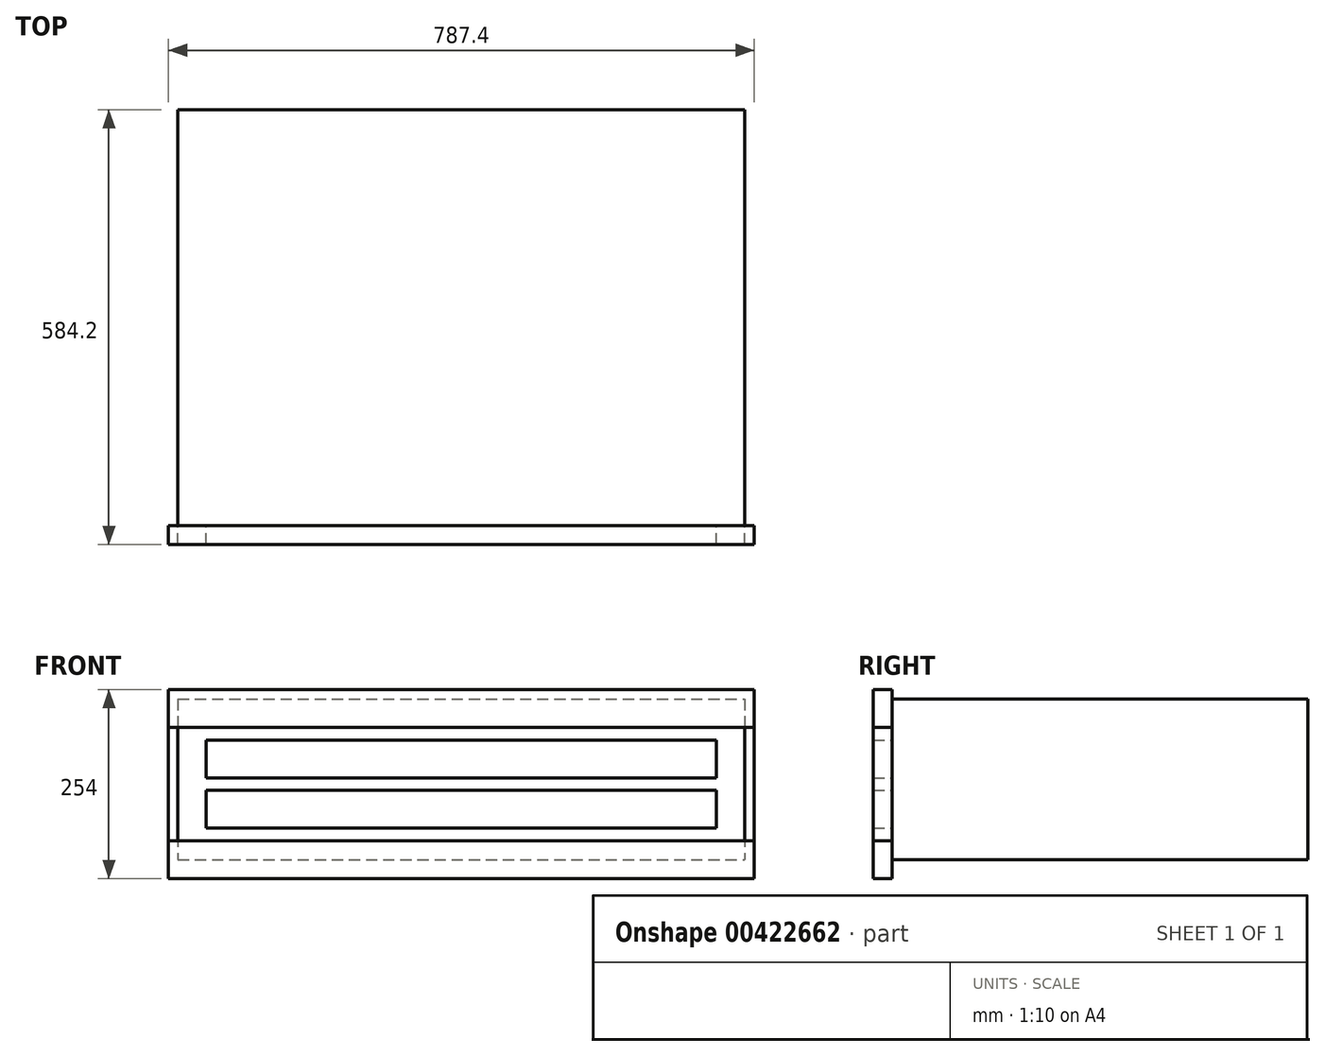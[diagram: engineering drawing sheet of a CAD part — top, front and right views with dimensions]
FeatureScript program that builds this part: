
annotation { "Feature Type Name" : "Feature", "Feature Type Description" : "" }
export const myFeature = defineFeature(function(context is Context, id is Id, definition is map)
    precondition{}
    {
        {
            var Q0;
            Q0=qCreatedBy(makeId("Front.planeOp"),FACE);
            var sketch = newSketch(context, id + "F0", { "sketchPlane" : qUnion([Q0])});
            skLineSegment(sketch, "E0.bottom", {"start": v(0, 0) * mm, "end": v(774.7, 0) * mm, "construction": true});
            skLineSegment(sketch, "E0.top", {"start": v(0, 279.4) * mm, "end": v(774.7, 279.4) * mm, "construction": true});
            skLineSegment(sketch, "E0.left", {"start": v(0, 0) * mm, "end": v(0, 279.4) * mm, "construction": true});
            skLineSegment(sketch, "E0.right", {"start": v(774.7, 0) * mm, "end": v(774.7, 279.4) * mm, "construction": true});
            skLineSegment(sketch, "E1", {"start": v(0, 50.8) * mm, "end": v(774.7, 50.8) * mm});
            skLineSegment(sketch, "E2", {"start": v(0, 266.7) * mm, "end": v(774.7, 266.7) * mm});
            skLineSegment(sketch, "E3", {"start": v(774.7, 266.7) * mm, "end": v(768.35, 266.7) * mm, "construction": true});
            skLineSegment(sketch, "E4", {"start": v(768.35, 266.7) * mm, "end": v(768.35, 50.8) * mm});
            skLineSegment(sketch, "E5", {"start": v(6.35, 266.7) * mm, "end": v(6.35, 50.8) * mm});
            skSolve(sketch);
        }
        {
            var Q0;
            {var subQ0=sQuery(id+"F0.wireOp",EDGE,"E4");Q0=makeQuery(id+"F0.imprint","IMPRINT",FACE,{"disambiguationData":[TD([[makeQuery(id+"F0.imprint","IMPRINT",EDGE,{"derivedFrom":subQ0}),-1.0]])]});}
            var Q1;
            Q1=sQuery(id+"F0.wireOp",EDGE,"E5");
            var Q2;
            Q2=sQuery(id+"F0.wireOp",EDGE,"E2");
            var Q3;
            Q3=sQuery(id+"F0.wireOp",EDGE,"E1");
            var Q4;
            Q4=sQuery(id+"F0.wireOp",EDGE,"E4");
            extrude(context, id + "F1", {"entities" : qUnion([Q0]), "surfaceEntities" : qUnion([Q1, Q2, Q3, Q4]), "oppositeDirection" : true, "depth" : 558.8 * mm});
        }
        {
            var Q0;
            Q0=makeQuery(id+"F1.opExtrude","CAP_FACE",FACE,{"disambiguationData":[OSD([sQuery(id+"F0.wireOp",EDGE,"E1"),sQuery(id+"F0.wireOp",EDGE,"E2"),sQuery(id+"F0.wireOp",EDGE,"E4"),sQuery(id+"F0.wireOp",EDGE,"E5")])],"isStart":true});
            var sketch = newSketch(context, id + "F2", { "sketchPlane" : qUnion([Q0])});
            skLineSegment(sketch, "E6.bottom", {"start": v(-6.35, 228.6) * mm, "end": v(781.05, 228.6) * mm});
            skLineSegment(sketch, "E6.top", {"start": v(-6.35, 279.4) * mm, "end": v(781.05, 279.4) * mm});
            skLineSegment(sketch, "E6.left", {"start": v(-6.35, 228.6) * mm, "end": v(-6.35, 279.4) * mm});
            skLineSegment(sketch, "E6.right", {"start": v(781.05, 228.6) * mm, "end": v(781.05, 279.4) * mm});
            skLineSegment(sketch, "E7.bottom", {"start": v(44.45, 211.67) * mm, "end": v(730.25, 211.67) * mm});
            skLineSegment(sketch, "E7.top", {"start": v(44.45, 160.87) * mm, "end": v(730.25, 160.87) * mm});
            skLineSegment(sketch, "E7.left", {"start": v(44.45, 211.67) * mm, "end": v(44.45, 160.87) * mm});
            skLineSegment(sketch, "E7.right", {"start": v(730.25, 211.67) * mm, "end": v(730.25, 160.87) * mm});
            skLineSegment(sketch, "E8.bottom", {"start": v(44.45, 143.93) * mm, "end": v(730.25, 143.93) * mm});
            skLineSegment(sketch, "E8.top", {"start": v(44.45, 93.13) * mm, "end": v(730.25, 93.13) * mm});
            skLineSegment(sketch, "E8.left", {"start": v(44.45, 143.93) * mm, "end": v(44.45, 93.13) * mm});
            skLineSegment(sketch, "E8.right", {"start": v(730.25, 143.93) * mm, "end": v(730.25, 93.13) * mm});
            skLineSegment(sketch, "E9.bottom", {"start": v(-6.35, 76.2) * mm, "end": v(781.05, 76.2) * mm});
            skLineSegment(sketch, "E9.top", {"start": v(-6.35, 25.4) * mm, "end": v(781.05, 25.4) * mm});
            skLineSegment(sketch, "E9.left", {"start": v(-6.35, 76.2) * mm, "end": v(-6.35, 25.4) * mm});
            skLineSegment(sketch, "E9.right", {"start": v(781.05, 76.2) * mm, "end": v(781.05, 25.4) * mm});
            skLineSegment(sketch, "E10", {"start": v(387.35, 228.6) * mm, "end": v(387.35, 211.67) * mm, "construction": true});
            skLineSegment(sketch, "E11", {"start": v(387.35, 160.87) * mm, "end": v(387.35, 143.93) * mm, "construction": true});
            skLineSegment(sketch, "E12", {"start": v(387.35, 93.13) * mm, "end": v(387.35, 76.2) * mm, "construction": true});
            skLineSegment(sketch, "E13.bottom", {"start": v(-6.35, 228.6) * mm, "end": v(44.45, 228.6) * mm});
            skLineSegment(sketch, "E13.top", {"start": v(-6.35, 76.2) * mm, "end": v(44.45, 76.2) * mm});
            skLineSegment(sketch, "E13.left", {"start": v(-6.35, 228.6) * mm, "end": v(-6.35, 76.2) * mm});
            skLineSegment(sketch, "E13.right", {"start": v(44.45, 228.6) * mm, "end": v(44.45, 76.2) * mm});
            skLineSegment(sketch, "E14.bottom", {"start": v(781.05, 76.2) * mm, "end": v(730.25, 76.2) * mm});
            skLineSegment(sketch, "E14.top", {"start": v(781.05, 228.6) * mm, "end": v(730.25, 228.6) * mm});
            skLineSegment(sketch, "E14.left", {"start": v(781.05, 76.2) * mm, "end": v(781.05, 228.6) * mm});
            skLineSegment(sketch, "E14.right", {"start": v(730.25, 76.2) * mm, "end": v(730.25, 228.6) * mm});
            skSolve(sketch);
        }
        {
            var Q0;
            Q0=makeQuery(id+"F2.imprint","IMPRINT",FACE,{"disambiguationData":[TD([[makeQuery(id+"F2.imprint","IMPRINT",EDGE,{"derivedFrom":sQuery(id+"F2.wireOp",EDGE,"E6.top")}),-1.0]])]});
            var Q1;
            {var subQ1=sQuery(id+"F2.wireOp",EDGE,"E6.bottom");Q1=makeQuery(id+"F2.imprint","IMPRINT",FACE,{"disambiguationData":[TD([[makeQuery(id+"F2.imprint","IMPRINT",EDGE,{"derivedFrom":subQ1}),1.0]])]});}
            extrude(context, id + "F3", {"entities" : qUnion([Q0, Q1]), "depth" : 25.4 * mm});
        }
        {
            var Q0;
            {var subQ0=sQuery(id+"F2.wireOp",EDGE,"E14.left");Q0=makeQuery(id+"F2.imprint","IMPRINT",FACE,{"disambiguationData":[TD([[makeQuery(id+"F2.imprint","IMPRINT",EDGE,{"derivedFrom":subQ0}),1.0]])]});}
            var Q1;
            {var subQ0=sQuery(id+"F2.wireOp",EDGE,"E14.right");var subQ9=makeQuery(id+"F2.imprint","INTERSECT",VERTEX,{"derivedFrom":[sQuery(id+"F2.wireOp",EDGE,"E8.bottom"),subQ0]});Q1=makeQuery(id+"F2.imprint","IMPRINT",FACE,{"disambiguationData":[TD([[makeQuery(id+"F2.imprint","IMPRINT",EDGE,{"disambiguationData":[TD([[subQ9,1.0]])],"derivedFrom":subQ0}),-1.0]])]});}
            extrude(context, id + "F4", {"entities" : qUnion([Q0, Q1]), "depth" : 25.4 * mm});
        }
        {
            var Q0;
            {var subQ0=sQuery(id+"F2.wireOp",EDGE,"E7.bottom");Q0=makeQuery(id+"F2.imprint","IMPRINT",FACE,{"disambiguationData":[TD([[makeQuery(id+"F2.imprint","IMPRINT",EDGE,{"derivedFrom":subQ0}),-1.0]])]});}
            extrude(context, id + "F5", {"entities" : qUnion([Q0]), "depth" : 25.4 * mm});
        }
        {
            var Q0;
            {var subQ0=sQuery(id+"F2.wireOp",EDGE,"E8.bottom");Q0=makeQuery(id+"F2.imprint","IMPRINT",FACE,{"disambiguationData":[TD([[makeQuery(id+"F2.imprint","IMPRINT",EDGE,{"derivedFrom":subQ0}),-1.0]])]});}
            extrude(context, id + "F6", {"entities" : qUnion([Q0]), "depth" : 25.4 * mm});
        }
        {
            var Q0;
            Q0=makeQuery(id+"F2.imprint","IMPRINT",FACE,{"disambiguationData":[TD([[makeQuery(id+"F2.imprint","IMPRINT",EDGE,{"derivedFrom":sQuery(id+"F2.wireOp",EDGE,"E9.top")}),1.0]])]});
            var Q1;
            {var subQ2=sQuery(id+"F2.wireOp",EDGE,"E9.bottom");Q1=makeQuery(id+"F2.imprint","IMPRINT",FACE,{"disambiguationData":[TD([[makeQuery(id+"F2.imprint","IMPRINT",EDGE,{"derivedFrom":subQ2}),-1.0]])]});}
            extrude(context, id + "F7", {"entities" : qUnion([Q0, Q1]), "depth" : 25.4 * mm});
        }
        {
            var Q0;
            {var subQ0=sQuery(id+"F2.wireOp",EDGE,"E13.right");var subQ3=makeQuery(id+"F2.imprint","INTERSECT",VERTEX,{"derivedFrom":[sQuery(id+"F2.wireOp",EDGE,"E7.bottom"),subQ0]});Q0=makeQuery(id+"F2.imprint","IMPRINT",FACE,{"disambiguationData":[TD([[makeQuery(id+"F2.imprint","IMPRINT",EDGE,{"disambiguationData":[TD([[subQ3,-1.0]])],"derivedFrom":subQ0}),-1.0]])]});}
            var Q1;
            {var subQ0=sQuery(id+"F2.wireOp",EDGE,"E13.left");Q1=makeQuery(id+"F2.imprint","IMPRINT",FACE,{"disambiguationData":[TD([[makeQuery(id+"F2.imprint","IMPRINT",EDGE,{"derivedFrom":subQ0}),1.0]])]});}
            extrude(context, id + "F8", {"entities" : qUnion([Q0, Q1]), "depth" : 25.4 * mm});
        }
    });
